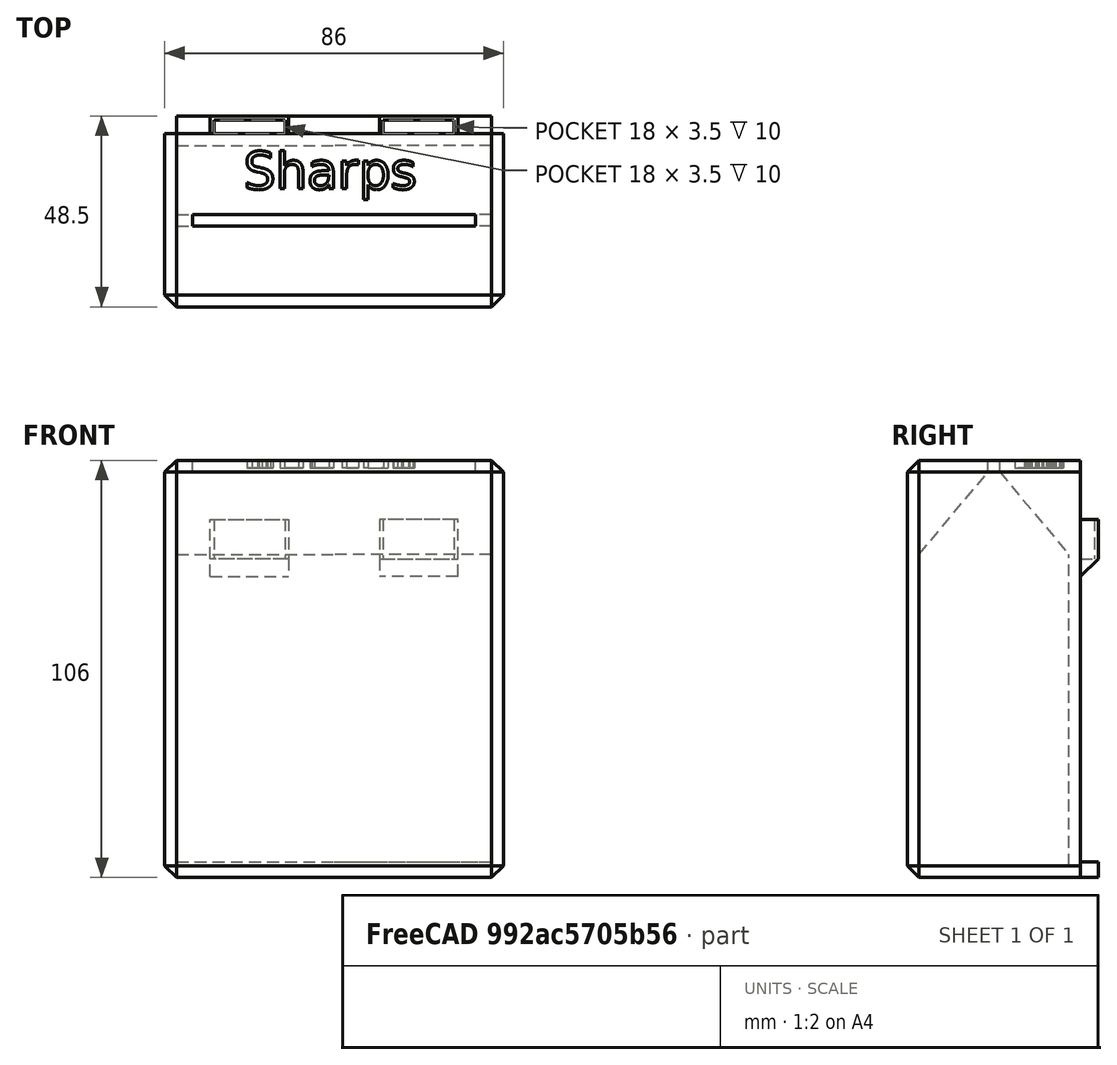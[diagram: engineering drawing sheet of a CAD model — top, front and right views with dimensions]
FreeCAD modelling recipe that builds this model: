
FCSTD DOCUMENT  (FreeCAD 0.19R14555 (Git shallow))
Label: Sharps
License: All rights reserved
LicenseURL: http://en.wikipedia.org/wiki/All_rights_reserved
objects: Sketcher::SketchObject×7, PartDesign::Pad×5, PartDesign::Pocket×3, PartDesign::Mirrored×2, PartDesign::Thickness×1, PartDesign::Chamfer×1, Part::Part2DObjectPython×1, PartDesign::ShapeBinder×1, PartDesign::Body×1, Mesh::Feature×1
note: 32 computed .brp shape members not serialized (recipe doc carries the construction recipe); baked Part::Feature solids carry a one-line shape summary decoded from their .brp

FEATURE [Sketcher::SketchObject] Sketch
  FullyConstrained = true
  MapMode = 5
  Support = -> [XY_Plane]
  sketch-geometry (4):
    g0: LineSegment StartX=0 StartY=0 StartZ=0 EndX=40 EndY=0 EndZ=0
    g1: LineSegment StartX=40 StartY=0 StartZ=0 EndX=40 EndY=38 EndZ=0
    g2: LineSegment StartX=40 StartY=38 StartZ=0 EndX=0 EndY=38 EndZ=0
    g3: LineSegment StartX=0 StartY=38 StartZ=0 EndX=0 EndY=0 EndZ=0
  constraints (11):
    c: Coincident(g0,g1)
    c: Coincident(g1,g2)
    c: Coincident(g2,g3)
    c: Coincident(g3,g0)
    c: Horizontal(g0)
    c: Horizontal(g2)
    c: Vertical(g1)
    c: Vertical(g3)
    c: Coincident(g0,g-1)
    c: DistanceX(g1) = 40
    c: DistanceY(g1) = 38
FEATURE [PartDesign::Pad] Pad
  Direction = (1,1,1)
  Length = 100
  Length2 = 100
  Profile = -> Sketch
  Type = 0
FEATURE [PartDesign::Thickness] Thickness
  Base = -> Pad [Face2]
  BaseFeature = -> Pad
  Intersection = false
  Join = 1
  Mode = 0
  SupportTransform = false
  Value = 3
FEATURE [Sketcher::SketchObject] Sketch001
  ExternalGeometry = -> [Thickness]
  FullyConstrained = true
  MapMode = 5
  Placement = pos=(0,0,0) rot=(0.57735,0.57735,0.57735;2.0944rad)
  Support = -> [Thickness]
  sketch-geometry (7):
    g0: LineSegment StartX=0 StartY=79.1443 StartZ=0 EndX=17.5 EndY=100 EndZ=0
    g1: LineSegment StartX=0 StartY=100 StartZ=0 EndX=17.5 EndY=100 EndZ=0
    g2: LineSegment StartX=0 StartY=79.1443 StartZ=0 EndX=0 EndY=100 EndZ=0
    g3: LineSegment StartX=20.5 StartY=100 StartZ=0 EndX=38 EndY=79.1443 EndZ=0
    g4: LineSegment StartX=38 StartY=100 StartZ=0 EndX=38 EndY=79.1443 EndZ=0
    g5: LineSegment StartX=38 StartY=100 StartZ=0 EndX=20.5 EndY=100 EndZ=0
    g6: LineSegment StartX=17.5 StartY=100 StartZ=0 EndX=20.5 EndY=100 EndZ=0
  constraints (18):
    c: PointOnObject(g0,g-4)
    c: PointOnObject(g0,g-3)
    c: Coincident(g1,g-4)
    c: Coincident(g1,g0)
    c: Coincident(g2,g0)
    c: Coincident(g2,g1)
    c: PointOnObject(g3,g-3)
    c: PointOnObject(g3,g-5)
    c: Coincident(g4,g-5)
    c: Coincident(g4,g3)
    c: Coincident(g5,g4)
    c: Coincident(g5,g3)
    c: Coincident(g6,g0)
    c: Coincident(g6,g3)
    c: DistanceX(g6,g6) = 3
    c: Equal(g1,g5)
    c: Equal(g2,g4)
    c: Angle(g0,g2) = 0.698132
FEATURE [PartDesign::Pad] Pad001
  BaseFeature = -> Thickness
  Direction = (1,1,1)
  Length = 10
  Length2 = 100
  Profile = -> Sketch001
  Type = 3
  UpToFace = -> Thickness [Face6]
FEATURE [Sketcher::SketchObject] Sketch002
  ExternalGeometry = -> [Pad001]
  FullyConstrained = true
  MapMode = 5
  Placement = pos=(0,0,100) rot=(1,0,0;3.14159rad)
  Support = -> [Pad001]
  sketch-geometry (5):
    g0: LineSegment StartX=4 StartY=-17.5 StartZ=0 EndX=40 EndY=-17.5 EndZ=0
    g1: LineSegment StartX=40 StartY=-17.5 StartZ=0 EndX=40 EndY=-20.5 EndZ=0
    g2: LineSegment StartX=40 StartY=-20.5 StartZ=0 EndX=4 EndY=-20.5 EndZ=0
    g3: LineSegment StartX=4 StartY=-20.5 StartZ=0 EndX=4 EndY=-17.5 EndZ=0
    g4: LineSegment StartX=0 StartY=-17.5 StartZ=0 EndX=4 EndY=-17.5 EndZ=0
  constraints (13):
    c: Coincident(g0,g1)
    c: Coincident(g1,g2)
    c: Coincident(g2,g3)
    c: Coincident(g3,g0)
    c: Horizontal(g0)
    c: Horizontal(g2)
    c: Vertical(g1)
    c: Vertical(g3)
    c: PointOnObject(g0,g-3)
    c: Coincident(g1,g-4)
    c: Coincident(g4,g-3)
    c: Coincident(g4,g0)
    c: DistanceX(g4,g4) = 4
FEATURE [PartDesign::Pocket] Pocket
  BaseFeature = -> Pad001
  Length = 0
  Length2 = 100
  Profile = -> Sketch002
  Type = 3
  UpToFace = -> Pad001 [Face14]
FEATURE [PartDesign::Mirrored] Mirrored
  BaseFeature = -> Pocket
  MirrorPlane = -> Pocket [Face5]
  Originals = -> [Thickness,Pad001,Pocket]
FEATURE [PartDesign::Chamfer] Chamfer
  Angle = 45
  Base = -> Mirrored [Edge42,Edge43,Edge60,Edge59,Edge68,Edge55,Edge54,Edge64,Edge52,Edge63]
  BaseFeature = -> Mirrored
  ChamferType = 0
  FlipDirection = false
  Size = 3
  Size2 = 1
  SupportTransform = false
FEATURE [Sketcher::SketchObject] Sketch007
  ExternalGeometry = -> [Chamfer]
  FullyConstrained = true
  MapMode = 5
  Placement = pos=(0,41,0) rot=(0,0.707107,0.707107;3.14159rad)
  Support = -> [Chamfer]
  sketch-geometry (4):
    g0: LineSegment StartX=-80 StartY=-3 StartZ=0 EndX=0 EndY=-3 EndZ=0
    g1: LineSegment StartX=0 StartY=-3 StartZ=0 EndX=0 EndY=1 EndZ=0
    g2: LineSegment StartX=0 StartY=1 StartZ=0 EndX=-80 EndY=1 EndZ=0
    g3: LineSegment StartX=-80 StartY=1 StartZ=0 EndX=-80 EndY=-3 EndZ=0
  constraints (10):
    c: Coincident(g0,g1)
    c: Coincident(g1,g2)
    c: Coincident(g2,g3)
    c: Coincident(g3,g0)
    c: Horizontal(g2)
    c: Vertical(g1)
    c: Vertical(g3)
    c: Coincident(g0,g-4)
    c: DistanceY(g3,g3) = 4
    c: Coincident(g0,g-3)
FEATURE [PartDesign::Pad] Pad005
  BaseFeature = -> Chamfer
  Direction = (1,1,1)
  Length = 4.5
  Length2 = 100
  Profile = -> Sketch007
  Type = 0
FEATURE [Sketcher::SketchObject] Sketch004
  ExternalGeometry = -> [Pad005]
  FullyConstrained = true
  MapMode = 5
  Placement = pos=(0,41,0) rot=(0,0.707107,0.707107;3.14159rad)
  Support = -> [Pad005]
  sketch-geometry (7):
    g0: LineSegment StartX=-8.5 StartY=88 StartZ=0 EndX=-28.5 EndY=88 EndZ=0
    g1: LineSegment StartX=-28.5 StartY=88 StartZ=0 EndX=-28.5 EndY=78 EndZ=0
    g2: LineSegment StartX=-28.5 StartY=78 StartZ=0 EndX=-8.5 EndY=78 EndZ=0
    g3: LineSegment StartX=-8.5 StartY=78 StartZ=0 EndX=-8.5 EndY=88 EndZ=0
    g4: LineSegment StartX=-28.5 StartY=88 StartZ=0 EndX=-40 EndY=88 EndZ=0
    g5: LineSegment StartX=-8.5 StartY=88 StartZ=0 EndX=3 EndY=88 EndZ=0
    g6: LineSegment StartX=-40 StartY=103 StartZ=0 EndX=-40 EndY=1 EndZ=0
  constraints (20):
    c: Coincident(g0,g1)
    c: Coincident(g1,g2)
    c: Coincident(g2,g3)
    c: Coincident(g3,g0)
    c: Horizontal(g0)
    c: Horizontal(g2)
    c: Vertical(g1)
    c: Vertical(g3)
    c: DistanceX(g2,g2) = 20
    c: DistanceY(g3,g3) = 10
    c: DistanceY(g0,g-3) = 15
    c: Coincident(g4,g0)
    c: PointOnObject(g4,g-5)
    c: Horizontal(g4)
    c: Coincident(g5,g0)
    c: PointOnObject(g5,g-4)
    c: Equal(g4,g5)
    c: Horizontal(g5)
    c: Coincident(g6,g-5)
    c: Coincident(g6,g-5)
FEATURE [PartDesign::Pad] Pad006  label="MagnetPad"
  BaseFeature = -> Pad005
  Direction = (1,1,1)
  Length = 4.5
  Length2 = 100
  Profile = -> Sketch004
  Type = 0
FEATURE [Sketcher::SketchObject] Sketch008
  ExternalGeometry = -> [Pad006]
  FullyConstrained = true
  MapMode = 5
  Placement = pos=(0,1.94e-14,88) rot=(0,0,1;0rad)
  Support = -> [Pad006]
  sketch-geometry (7):
    g0: LineSegment StartX=27.5 StartY=41 StartZ=0 EndX=9.5 EndY=41 EndZ=0
    g1: LineSegment StartX=9.5 StartY=41 StartZ=0 EndX=9.5 EndY=44.5 EndZ=0
    g2: LineSegment StartX=9.5 StartY=44.5 StartZ=0 EndX=27.5 EndY=44.5 EndZ=0
    g3: LineSegment StartX=27.5 StartY=44.5 StartZ=0 EndX=27.5 EndY=41 EndZ=0
    g4: LineSegment StartX=28.5 StartY=41 StartZ=0 EndX=27.5 EndY=41 EndZ=0
    g5: LineSegment StartX=9.5 StartY=41 StartZ=0 EndX=8.5 EndY=41 EndZ=0
    g6: LineSegment StartX=27.5 StartY=44.5 StartZ=0 EndX=27.5 EndY=45.5 EndZ=0
  constraints (20):
    c: Coincident(g0,g1)
    c: Coincident(g1,g2)
    c: Coincident(g2,g3)
    c: Coincident(g3,g0)
    c: Horizontal(g0)
    c: Horizontal(g2)
    c: Vertical(g1)
    c: Vertical(g3)
    c: PointOnObject(g0,g-3)
    c: PointOnObject(g4,g3)
    c: Horizontal(g4)
    c: Coincident(g5,g0)
    c: Coincident(g5,g-3)
    c: Coincident(g6,g2)
    c: PointOnObject(g6,g-5)
    c: Vertical(g6)
    c: Equal(g4,g6)
    c: Equal(g6,g5)
    c: DistanceX(g4,g4) = 1
    c: Coincident(g4,g-4)
FEATURE [PartDesign::Pocket] Pocket001  label="MagnetPocket"
  BaseFeature = -> Pad006
  Length = 0
  Length2 = 100
  Profile = -> Sketch008
  Type = 3
  UpToFace = -> Pad006 [Face15]
FEATURE [Sketcher::SketchObject] Sketch009
  ExternalGeometry = -> [Pocket001]
  FullyConstrained = true
  MapMode = 5
  Placement = pos=(8.5,0,0) rot=(0.57735,-0.57735,-0.57735;2.0944rad)
  Support = -> [Pocket001]
  sketch-geometry (3):
    g0: LineSegment StartX=-41 StartY=78 StartZ=0 EndX=-45.5 EndY=78 EndZ=0
    g1: LineSegment StartX=-45.5 StartY=78 StartZ=0 EndX=-41 EndY=73.5 EndZ=0
    g2: LineSegment StartX=-41 StartY=73.5 StartZ=0 EndX=-41 EndY=78 EndZ=0
  constraints (7):
    c: Coincident(g-3,g0)
    c: Coincident(g0,g-3)
    c: Coincident(g0,g1)
    c: Coincident(g1,g2)
    c: Coincident(g2,g0)
    c: Vertical(g2)
    c: Angle(g2,g1) = 0.785398
FEATURE [PartDesign::Pad] Pad007  label="MagnetSupportPad"
  BaseFeature = -> Pocket001
  Direction = (1,1,1)
  Length = 10
  Length2 = 100
  Profile = -> Sketch009
  Type = 3
  UpToFace = -> Pocket001 [Face18]
FEATURE [PartDesign::Mirrored] Mirrored001
  BaseFeature = -> Pad007
  MirrorPlane = -> Sketch004 [Axis2]
  Originals = -> [Pad006,Pocket001,Pad007]
FEATURE [Part::Part2DObjectPython] ShapeString  # Draft 2D object (typed FeaturePython)
  AttachmentOffset = pos=(17,27,0) rot=(0,0,1;0rad)
  FontFile = <path>
  MapMode = 5
  Placement = pos=(17,27,103) rot=(0,0,1;0rad)
  Size = 10
  String = Sharps
  Support = -> [Mirrored001]
  Tracking = 0
FEATURE [PartDesign::ShapeBinder] ShapeBinder
  Placement = pos=(17,27,103) rot=(0,0,1;0rad)
  Support = -> [ShapeString]
  TraceSupport = true
FEATURE [PartDesign::Pocket] Pocket002
  BaseFeature = -> Mirrored001
  Length = 2
  Length2 = 100
  Profile = -> ShapeString
  Type = 0
FEATURE [PartDesign::Body] Body
  Group = -> [Sketch,Pad,Thickness,Sketch001,Pad001,Sketch002,Pocket,Mirrored,Chamfer,Pad005,Pad006,Pocket001,Sketch008,Sketch004,Sketch007,Sketch009,Pad007,Mirrored001,ShapeString,ShapeBinder,Pocket002]
  Origin = -> Origin
  Tip = -> Pocket002
FEATURE [Mesh::Feature] Mesh  label="SharpsRecepticle"
note: 1 file-system path scrubbed to <path> (originals preserved in the JSON sidecar)
